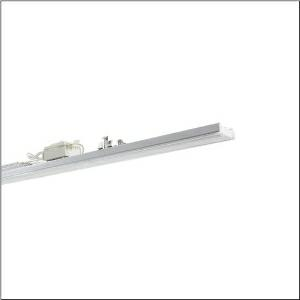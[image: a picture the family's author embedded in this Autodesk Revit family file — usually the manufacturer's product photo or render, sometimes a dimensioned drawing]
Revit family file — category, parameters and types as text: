
# Revit family: licross_r__11_recessed_extreme_ho_51te18dn4c5me_7eea
name_source: partatom
category: Lighting Fixtures
units: mm (PartAtom-declared; Revit-internal decimal feet)

## family parameters
Cut with Voids When Loaded = No
Host = Face
Light Source = No
Part Type = Normal
Room Calculation Point = No
Round Connector Dimension = Use Diameter
Shared = No

## types (1)
- --- (1 x LED, 12830 lm, 70.5 W, 4000K)
    Apparent Load = 71 VA
    CIE Flux Codes = 78 94 99 100 100
    Color Rendering = 80
    Color Temperature = 4000K
    Default Elevation = 1800 mm
    Description = Licross® 11 Recessed extreme HO, luminaire insert, of sheet steel, galvanised, coil coated, white, length: 1.500mm, width: 66mm, height: 67mm, LED rated luminous flux: 12.830lm, light colour: 840, control gear: DALI 2, with plug, 5-pole, with phase selection, mains connection: 220..240V, AC, 50/60Hz, rated input power: 71W, internal wiring halogen-free, primary light control with lens, of plastic, primary optical cover: cover, of PMMA, light emission: direct distribution, primary light characteristic: symmetric, protection rating (complete): IP54, insulation class (complete): insulation class I (protective earthing), certification: CE, ENEC, VDE, UKCA, protection symbol: D if used in an environment with non-conductive dust loads with corresponding accessories, impact resistance: IK06, permissible ambient temperature for indoor applications: -25..+45°C, corresponds to IFS (International Featured Standards) requirements for safety and quality in the food industry, reducing of maximum allowable ambient temperature of 5°C with ceiling mounting, LABS conformity tested according to VDMA 24364:2018-05, packaging unit: 1 piece
    Height = 58 mm
    Lamp = 1 x LED
    Lamp Light Flux = 12830 lm
    Lamp Power = 70.5 W
    Lamp count = 1
    Length = 1500 mm
    Luminous efficacy = 182 lm/W
    Manufacturer = Siteco
    ModVariant = No
    Model = 51TE18DN4C5ME
    Mounting Place = Ceiling
    Mounting Type = Pendant
    Number of Poles = 1
    OnlyDefault = Yes
    Power Factor = 1
    Product Name = Licross® 11 Recessed extreme HO
    Product group = luminaire insert | ceiling pendant
    ProductGroupID = 902
    Protection Class = Protection class I
    Protection Degree = IP 54
    RLX_Detail_Level = 1
    RLX_Emergency_Light_Flux = 0 lm
    RLX_Emergency_Type = 0
    RLX_Emergency_Type_DB = No
    RlxData = <blob elided: 24653 chars, md5=3d4c8ada>
    Socket = socket
    Standby Power = 0 W
    System Light Flux = 12830 lm
    System Power = 71 W
    Type Comments = factory setting: luminous flux: 100 % | dim-lin: 254 | 479 mA
    Type Image = l_1296930.jpg
    URL = http://relux.com
    VarID = @adj_111375
    Voltage = 0 V
    Weight = 0.00 kg
    Width = 66 mm

## geometry (parser evidence)
native form markers: Blend x4, Sweep x11
no freeform markers — native parametric forms only
